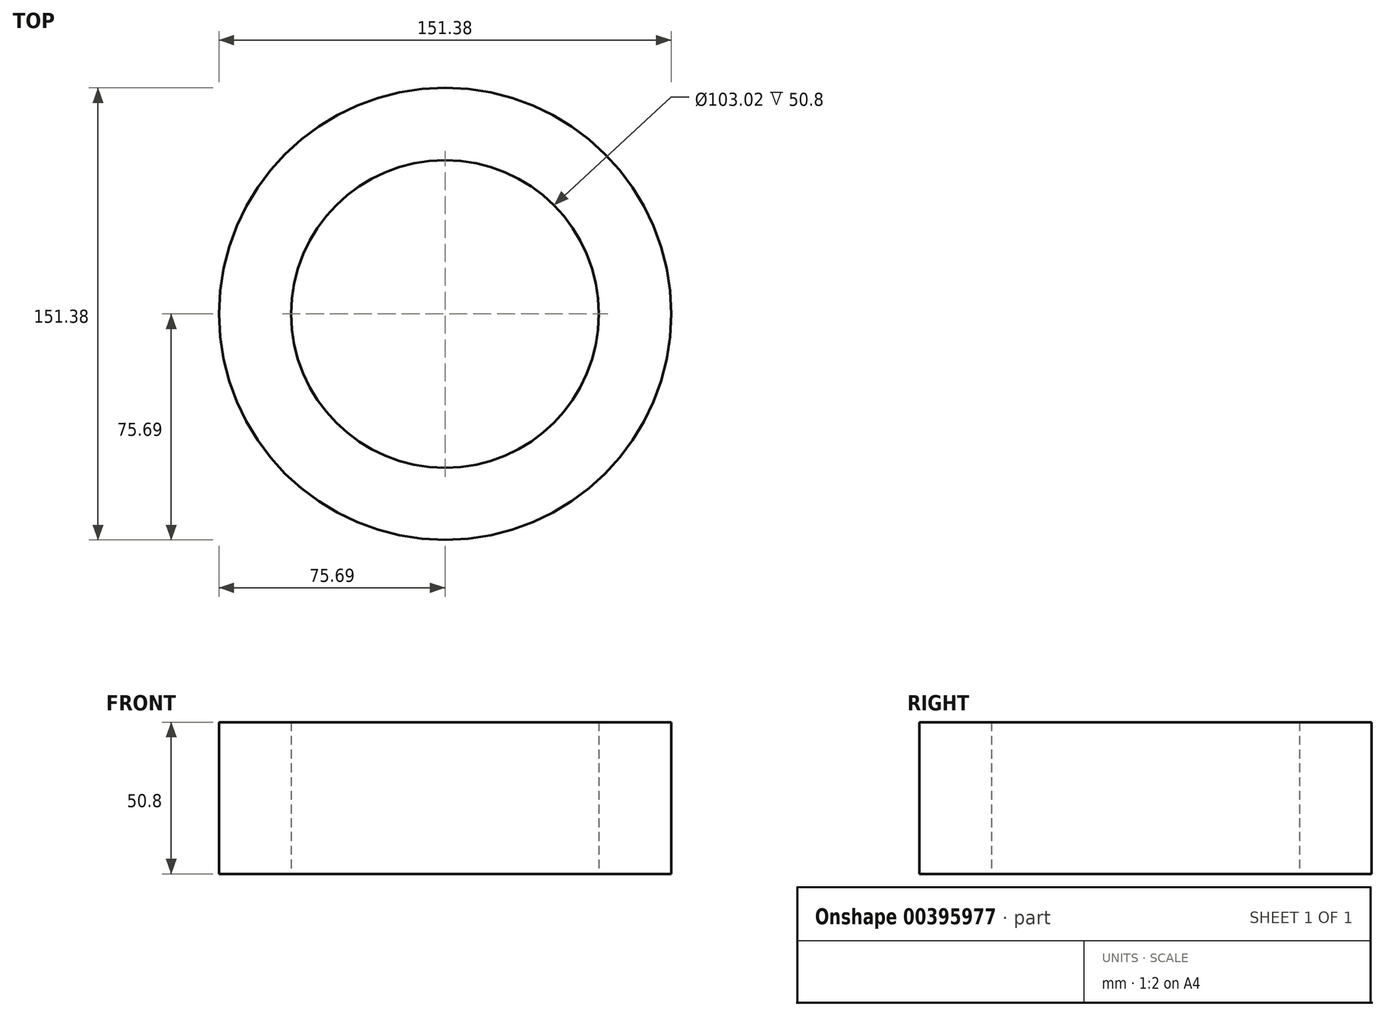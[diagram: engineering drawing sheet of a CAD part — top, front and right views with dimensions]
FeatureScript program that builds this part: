
annotation { "Feature Type Name" : "Feature", "Feature Type Description" : "" }
export const myFeature = defineFeature(function(context is Context, id is Id, definition is map)
    precondition{}
    {
        {
            var Q0;
            Q0=qCreatedBy(makeId("Top.planeOp"),FACE);
            var sketch = newSketch(context, id + "F0", { "sketchPlane" : qUnion([Q0])});
            skCircle(sketch, "E0", {"center": v(0, 0) * mm, "radius": 75.69 * mm});
            skSolve(sketch);
        }
        {
            var Q0;
            Q0=makeQuery(id+"F0.imprint","IMPRINT",FACE,{"disambiguationData":[TD([[makeQuery(id+"F0.imprint","IMPRINT",EDGE,{"derivedFrom":sQuery(id+"F0.wireOp",EDGE,"E0")}),1.0]])]});
            extrude(context, id + "F1", {"entities" : qUnion([Q0]), "depth" : 25.4 * mm});
        }
        {
            var Q0;
            Q0=makeQuery(id+"F1.opExtrude","CAP_FACE",FACE,{"disambiguationData":[OSD([sQuery(id+"F0.wireOp",EDGE,"E0")])],"isStart":true});
            extrude(context, id + "F2", {"entities" : qUnion([Q0]), "operationType" : NewBodyOperationType.ADD, "depth" : 25.4 * mm});
        }
        {
            var Q0;
            Q0=qCreatedBy(makeId("Top.planeOp"),FACE);
            var sketch = newSketch(context, id + "F3", { "sketchPlane" : qUnion([Q0])});
            skCircle(sketch, "E1", {"center": v(0, 0) * mm, "radius": 51.22 * mm});
            skSolve(sketch);
        }
        {
            var Q0;
            Q0=sQuery(id+"F3.wireOp",EDGE,"E1");
            extrude(context, id + "F4", {"bodyType" : ToolBodyType.SURFACE, "surfaceEntities" : qUnion([Q0]), "depth" : 25.4 * mm});
        }
        {
            var Q0;
            Q0 = qSketchRegion(id + "F3", true);
            extrude(context, id + "F5", {"entities" : qUnion([Q0]), "operationType" : NewBodyOperationType.ADD, "oppositeDirection" : true, "depth" : 25.4 * mm});
        }
        {
            var Q0;
            Q0=sQuery(id+"F3.wireOp",EDGE,"E1");
            extrude(context, id + "F6", {"bodyType" : ToolBodyType.SURFACE, "surfaceEntities" : qUnion([Q0]), "depth" : 25.4 * mm});
        }
        {
            var Q0;
            Q0=makeQuery(id+"F2.opExtrude","CAP_FACE",FACE,{"disambiguationData":[OSD([sQuery(id+"F0.wireOp",EDGE,"E0")])],"isStart":false});
            var sketch = newSketch(context, id + "F7", { "sketchPlane" : qUnion([Q0])});
            skCircle(sketch, "E2", {"center": v(0, 0) * mm, "radius": 51.5 * mm});
            skSolve(sketch);
        }
        {
            var Q0;
            Q0=makeQuery(id+"F7.imprint","IMPRINT",FACE,{"disambiguationData":[TD([[makeQuery(id+"F7.imprint","IMPRINT",EDGE,{"derivedFrom":sQuery(id+"F7.wireOp",EDGE,"E2")}),1.0]])]});
            extrude(context, id + "F8", {"entities" : qUnion([Q0]), "operationType" : NewBodyOperationType.REMOVE, "endBound" : BoundingType.THROUGH_ALL, "oppositeDirection" : true, "depth" : 25.4 * mm});
        }
    });
